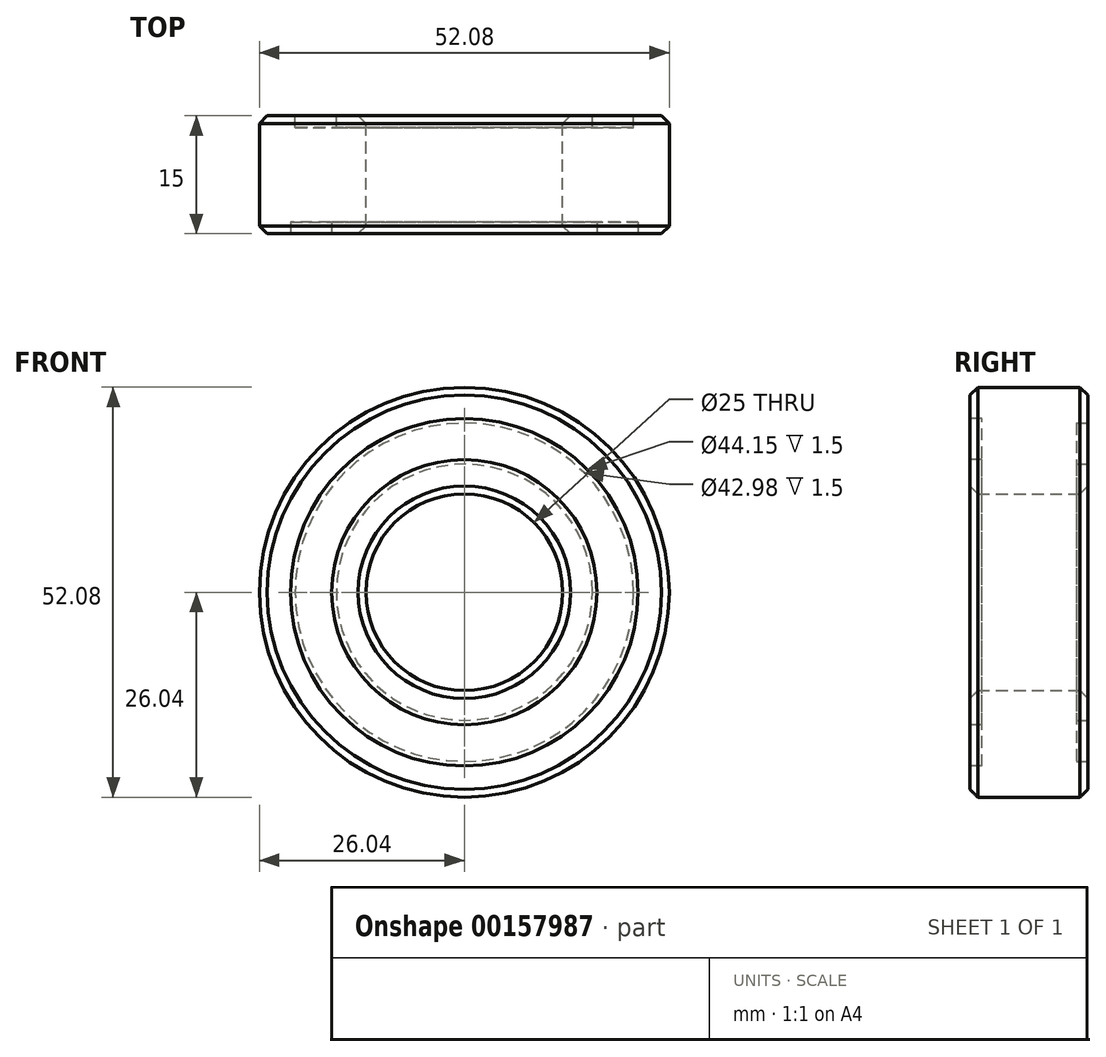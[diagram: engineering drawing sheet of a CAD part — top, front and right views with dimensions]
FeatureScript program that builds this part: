
annotation { "Feature Type Name" : "Feature", "Feature Type Description" : "" }
export const myFeature = defineFeature(function(context is Context, id is Id, definition is map)
    precondition{}
    {
        {
            var Q0;
            Q0=qCreatedBy(makeId("Front.planeOp"),FACE);
            var sketch = newSketch(context, id + "F0", { "sketchPlane" : qUnion([Q0])});
            skCircle(sketch, "E0", {"center": v(0, 0) * mm, "radius": 12.5 * mm});
            skCircle(sketch, "E1", {"center": v(0, 0) * mm, "radius": 26.04 * mm});
            skSolve(sketch);
        }
        {
            var Q0;
            Q0 = qSketchRegion(id + "F0", true);
            extrude(context, id + "F1", {"entities" : qUnion([Q0]), "depth" : 15 * mm});
        }
        {
            var Q0;
            Q0=makeQuery(id+"F1.opExtrude","CAP_FACE",FACE,{"disambiguationData":[OSD([sQuery(id+"F0.wireOp",EDGE,"E0"),sQuery(id+"F0.wireOp",EDGE,"E1")])],"isStart":false});
            var sketch = newSketch(context, id + "F2", { "sketchPlane" : qUnion([Q0])});
            skCircle(sketch, "E2", {"center": v(0, 0) * mm, "radius": 16.84 * mm});
            skCircle(sketch, "E3", {"center": v(0, 0) * mm, "radius": 22.07 * mm});
            skSolve(sketch);
        }
        {
            var Q0;
            Q0=makeQuery(id+"F2.imprint","IMPRINT",FACE,{"disambiguationData":[TD([[makeQuery(id+"F2.imprint","IMPRINT",EDGE,{"derivedFrom":sQuery(id+"F2.wireOp",EDGE,"E2")}),-1.0]])]});
            extrude(context, id + "F3", {"entities" : qUnion([Q0]), "operationType" : NewBodyOperationType.REMOVE, "oppositeDirection" : true, "depth" : 1.5 * mm});
        }
        {
            var Q0;
            Q0=makeQuery(id+"F1.opExtrude","CAP_FACE",FACE,{"disambiguationData":[OSD([sQuery(id+"F0.wireOp",EDGE,"E0"),sQuery(id+"F0.wireOp",EDGE,"E1")])],"isStart":true});
            var sketch = newSketch(context, id + "F4", { "sketchPlane" : qUnion([Q0])});
            skCircle(sketch, "E4", {"center": v(0, 0) * mm, "radius": 16.26 * mm});
            skCircle(sketch, "E5", {"center": v(0, 0) * mm, "radius": 21.5 * mm});
            skSolve(sketch);
        }
        {
            var Q0;
            Q0 = qSketchRegion(id + "F4", true);
            extrude(context, id + "F5", {"entities" : qUnion([Q0]), "operationType" : NewBodyOperationType.REMOVE, "oppositeDirection" : true, "depth" : 1.5 * mm});
        }
        {
            var Q0;
            Q0=makeQuery(id+"F1.opExtrude","CAP_EDGE",EDGE,{"disambiguationData":[OSD([sQuery(id+"F0.wireOp",EDGE,"E1")])],"isStart":true});
            var Q1;
            Q1=makeQuery(id+"F1.opExtrude","CAP_EDGE",EDGE,{"disambiguationData":[OSD([sQuery(id+"F0.wireOp",EDGE,"E1")])],"isStart":false});
            var Q2;
            Q2=makeQuery(id+"F1.opExtrude","CAP_EDGE",EDGE,{"disambiguationData":[OSD([sQuery(id+"F0.wireOp",EDGE,"E0")])],"isStart":false});
            var Q3;
            Q3=makeQuery(id+"F1.opExtrude","CAP_EDGE",EDGE,{"disambiguationData":[OSD([sQuery(id+"F0.wireOp",EDGE,"E0")])],"isStart":true});
            chamfer(context, id + "F6", {"entities" : qUnion([Q0, Q1, Q2, Q3]), "width" : 1 * mm, "tangentPropagation" : true});
        }
    });
